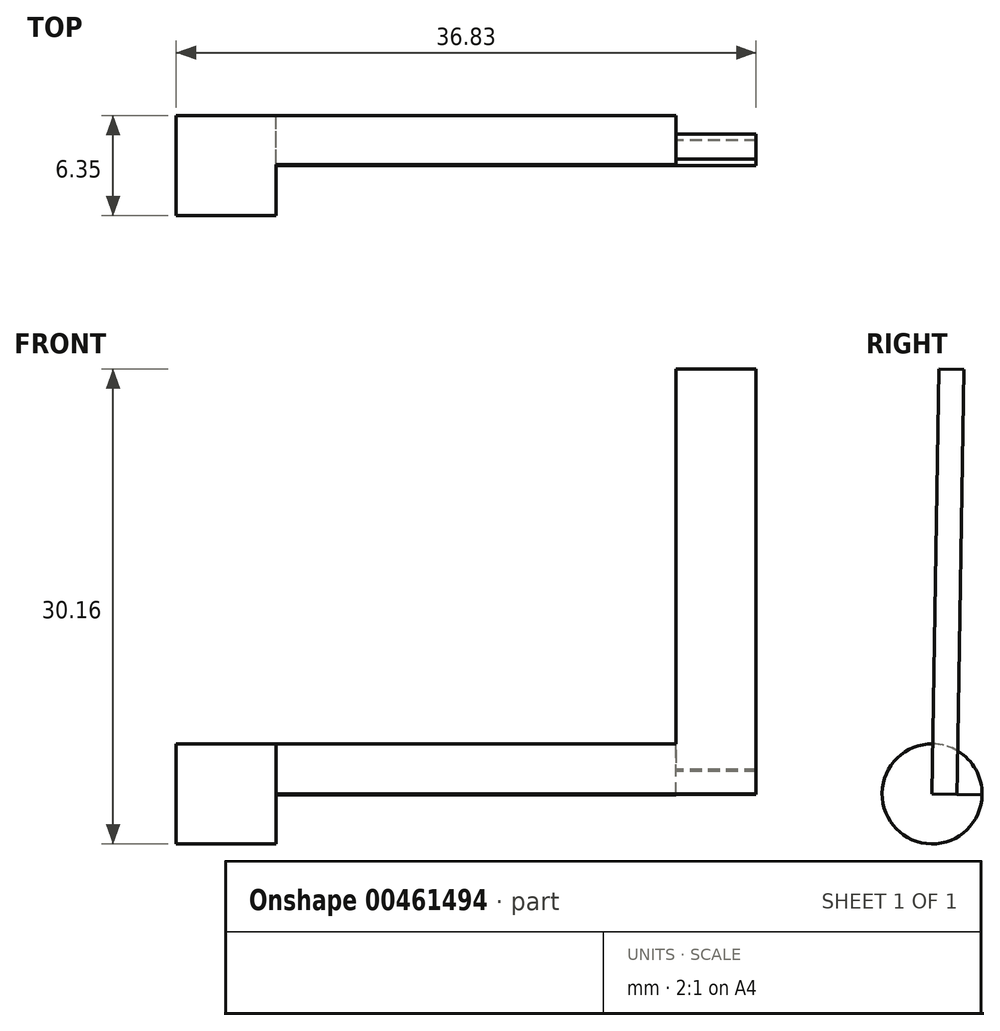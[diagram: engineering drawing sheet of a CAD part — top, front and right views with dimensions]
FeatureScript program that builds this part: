
annotation { "Feature Type Name" : "Feature", "Feature Type Description" : "" }
export const myFeature = defineFeature(function(context is Context, id is Id, definition is map)
    precondition{}
    {
        {
            var Q0;
            Q0=qCreatedBy(makeId("Right.planeOp"),FACE);
            var sketch = newSketch(context, id + "F0", { "sketchPlane" : qUnion([Q0])});
            skCircle(sketch, "E0", {"center": v(-37.77, 38.58) * mm, "radius": 3.18 * mm});
            skSolve(sketch);
        }
        {
            var Q0;
            Q0=makeQuery(id+"F0.imprint","IMPRINT",FACE,{"disambiguationData":[TD([[makeQuery(id+"F0.imprint","IMPRINT",EDGE,{"derivedFrom":sQuery(id+"F0.wireOp",EDGE,"E0")}),1.0]])]});
            extrude(context, id + "F1", {"entities" : qUnion([Q0]), "depth" : 6.35 * mm});
        }
        {
            var Q0;
            Q0=makeQuery(id+"F1.opExtrude","CAP_FACE",FACE,{"disambiguationData":[OSD([sQuery(id+"F0.wireOp",EDGE,"E0")])],"isStart":false});
            var sketch = newSketch(context, id + "F2", { "sketchPlane" : qUnion([Q0])});
            skCircle(sketch, "E1", {"center": v(-37.77, 38.58) * mm, "radius": 2.54 * mm});
            skSolve(sketch);
        }
        {
            var Q0;
            Q0=sQuery(id+"F2.wireOp",EDGE,"E1");
            extrude(context, id + "F3", {"bodyType" : ToolBodyType.SURFACE, "surfaceEntities" : qUnion([Q0]), "depth" : 25.4 * mm});
        }
        {
            var Q0;
            Q0=makeQuery(id+"F1.opExtrude","CAP_FACE",FACE,{"disambiguationData":[OSD([sQuery(id+"F0.wireOp",EDGE,"E0")])],"isStart":false});
            var sketch = newSketch(context, id + "F4", { "sketchPlane" : qUnion([Q0])});
            skLineSegment(sketch, "E2", {"start": v(-37.72, 41.76) * mm, "end": v(-37.77, 38.58) * mm});
            skLineSegment(sketch, "E3", {"start": v(-37.77, 38.58) * mm, "end": v(-34.6, 38.53) * mm});
            skSolve(sketch);
        }
        {
            var Q0;
            {var subQ0=sQuery(id+"F4.wireOp",EDGE,"E2");Q0=makeQuery(id+"F4.imprint","IMPRINT",FACE,{"disambiguationData":[TD([[makeQuery(id+"F4.imprint","IMPRINT",EDGE,{"derivedFrom":subQ0}),1.0]])]});}
            extrude(context, id + "F5", {"entities" : qUnion([Q0]), "operationType" : NewBodyOperationType.ADD, "depth" : 25.4 * mm});
        }
        {
            var Q0;
            Q0=makeQuery(id+"F5.opExtrude","CAP_FACE",FACE,{"disambiguationData":[OSD([sQuery(id+"F0.wireOp",EDGE,"E0"),sQuery(id+"F4.wireOp",EDGE,"E2"),sQuery(id+"F4.wireOp",EDGE,"E3")])],"isStart":false});
            var sketch = newSketch(context, id + "F6", { "sketchPlane" : qUnion([Q0])});
            skLineSegment(sketch, "E4", {"start": v(-36.18, 38.56) * mm, "end": v(-36.16, 40.01) * mm});
            skLineSegment(sketch, "E5", {"start": v(-37.75, 40.17) * mm, "end": v(-36.16, 40.15) * mm});
            skLineSegment(sketch, "E6", {"start": v(-36.16, 40.01) * mm, "end": v(-36.16, 40.15) * mm});
            skSolve(sketch);
        }
        {
            var Q0;
            {var subQ4=sQuery(id+"F6.wireOp",EDGE,"E4");Q0=makeQuery(id+"F6.imprint","IMPRINT",FACE,{"disambiguationData":[TD([[makeQuery(id+"F6.imprint","IMPRINT",EDGE,{"derivedFrom":subQ4}),1.0]])]});}
            extrude(context, id + "F7", {"entities" : qUnion([Q0]), "operationType" : NewBodyOperationType.ADD, "depth" : 5.08 * mm});
        }
        {
            var Q0;
            Q0=makeQuery(id+"F7.opExtrude","SWEPT_FACE",FACE,{"disambiguationData":[OSD([sQuery(id+"F6.wireOp",EDGE,"E5")])]});
            extrude(context, id + "F8", {"entities" : qUnion([Q0]), "operationType" : NewBodyOperationType.ADD, "depth" : 25.4 * mm});
        }
    });
